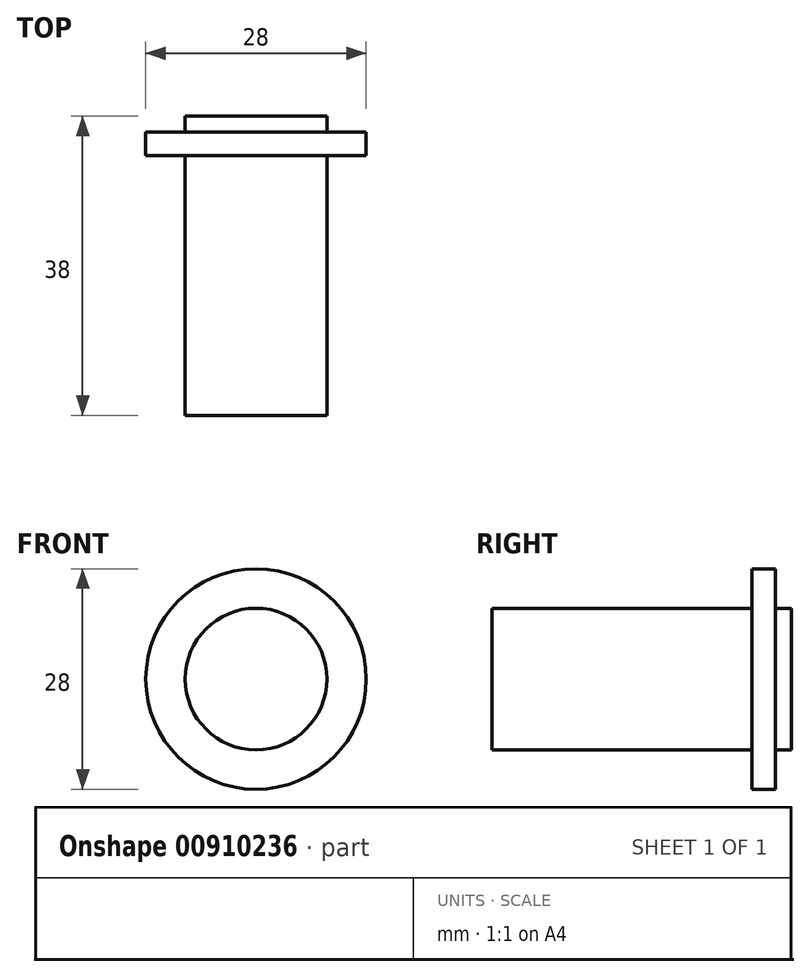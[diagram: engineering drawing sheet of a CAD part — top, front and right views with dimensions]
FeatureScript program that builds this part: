
annotation { "Feature Type Name" : "Feature", "Feature Type Description" : "" }
export const myFeature = defineFeature(function(context is Context, id is Id, definition is map)
    precondition{}
    {
        {
            var Q0;
            Q0=qCreatedBy(makeId("Front.planeOp"),FACE);
            var sketch = newSketch(context, id + "F0", { "sketchPlane" : qUnion([Q0])});
            skCircle(sketch, "E0", {"center": v(0, 0) * mm, "radius": 9 * mm});
            skCircle(sketch, "E1", {"center": v(0, 0) * mm, "radius": 14 * mm});
            skSolve(sketch);
        }
        {
            var Q0;
            Q0 = qSketchRegion(id + "F0", true);
            var Q1;
            Q1=makeQuery(id+"F0.imprint","IMPRINT",FACE,{"disambiguationData":[TD([[makeQuery(id+"F0.imprint","IMPRINT",EDGE,{"derivedFrom":sQuery(id+"F0.wireOp",EDGE,"E0")}),1.0]])]});
            extrude(context, id + "F1", {"entities" : qUnion([Q0, Q1]), "depth" : 3 * mm, "offsetDistance" : 25 * mm});
        }
        {
            var Q0;
            Q0=makeQuery(id+"F0.imprint","IMPRINT",FACE,{"disambiguationData":[TD([[makeQuery(id+"F0.imprint","IMPRINT",EDGE,{"derivedFrom":sQuery(id+"F0.wireOp",EDGE,"E0")}),1.0]])]});
            extrude(context, id + "F2", {"entities" : qUnion([Q0]), "operationType" : NewBodyOperationType.ADD, "depth" : 27 * mm, "offsetDistance" : 25 * mm});
        }
        {
            var Q0;
            Q0=makeQuery(id+"F0.imprint","IMPRINT",FACE,{"disambiguationData":[TD([[makeQuery(id+"F0.imprint","IMPRINT",EDGE,{"derivedFrom":sQuery(id+"F0.wireOp",EDGE,"E0")}),1.0]])]});
            extrude(context, id + "F3", {"entities" : qUnion([Q0]), "operationType" : NewBodyOperationType.ADD, "oppositeDirection" : true, "depth" : 2 * mm, "offsetDistance" : 25 * mm});
        }
        {
            var Q0;
            Q0=makeQuery(id+"F2.opExtrude","CAP_FACE",FACE,{"disambiguationData":[OSD([sQuery(id+"F0.wireOp",EDGE,"E0")])],"isStart":false});
            var sketch = newSketch(context, id + "F4", { "sketchPlane" : qUnion([Q0])});
            skCircle(sketch, "E2", {"center": v(0, 0) * mm, "radius": 3.75 * mm});
            skSolve(sketch);
        }
        {
            var Q0;
            Q0 = qSketchRegion(id + "F4", true);
            extrude(context, id + "F5", {"entities" : qUnion([Q0]), "operationType" : NewBodyOperationType.ADD, "depth" : 4 * mm, "offsetDistance" : 25 * mm});
        }
        {
            var Q0;
            Q0=makeQuery(id+"F2.opExtrude","CAP_FACE",FACE,{"disambiguationData":[OSD([sQuery(id+"F0.wireOp",EDGE,"E0")])],"isStart":false});
            var sketch = newSketch(context, id + "F6", { "sketchPlane" : qUnion([Q0])});
            skCircle(sketch, "E3", {"center": v(0, 0) * mm, "radius": 9 * mm});
            skSolve(sketch);
        }
        {
            var Q0;
            Q0=makeQuery(id+"F6.imprint","IMPRINT",FACE,{"disambiguationData":[TD([[makeQuery(id+"F6.imprint","IMPRINT",EDGE,{"derivedFrom":sQuery(id+"F6.wireOp",EDGE,"E3")}),1.0]])]});
            var sketch = newSketch(context, id + "F7", { "sketchPlane" : qUnion([Q0])});
            skCircle(sketch, "E4", {"center": v(0, 0) * mm, "radius": 9 * mm});
            skSolve(sketch);
        }
        {
            var Q0;
            Q0 = qSketchRegion(id + "F7", true);
            extrude(context, id + "F8", {"entities" : qUnion([Q0]), "operationType" : NewBodyOperationType.ADD, "depth" : 9 * mm, "offsetDistance" : 25 * mm});
        }
    });
